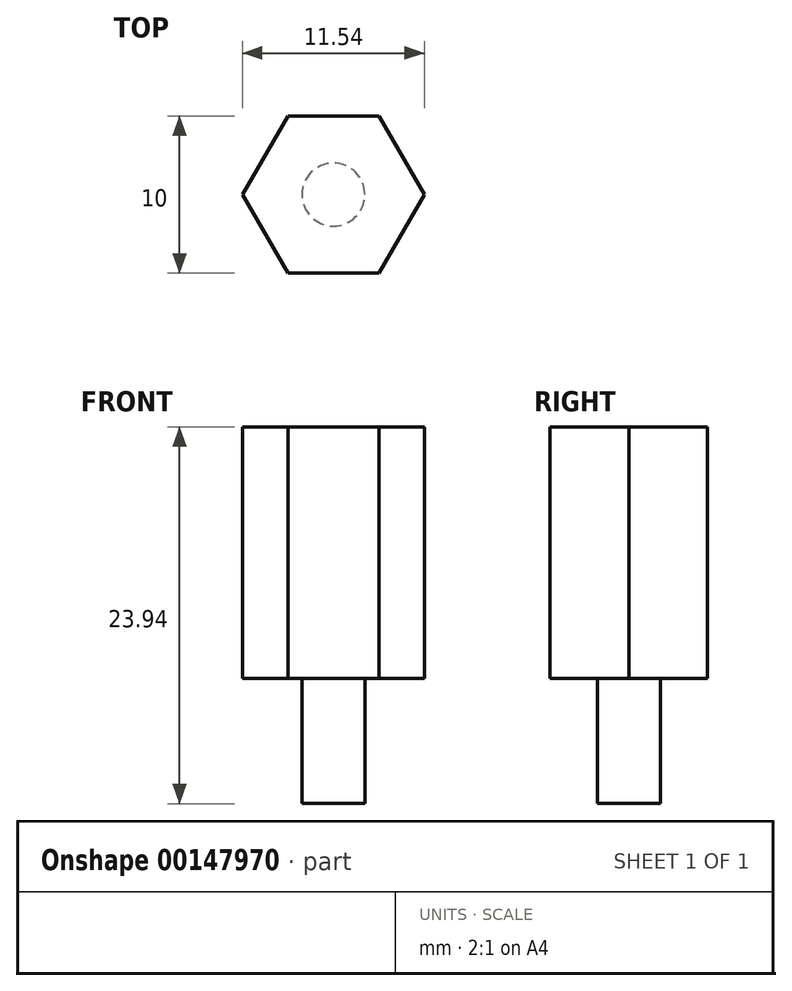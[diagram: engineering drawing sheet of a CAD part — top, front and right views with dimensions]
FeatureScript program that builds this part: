
annotation { "Feature Type Name" : "Feature", "Feature Type Description" : "" }
export const myFeature = defineFeature(function(context is Context, id is Id, definition is map)
    precondition{}
    {
        {
            var Q0;
            Q0=qCreatedBy(makeId("Top.planeOp"),FACE);
            var sketch = newSketch(context, id + "F0", { "sketchPlane" : qUnion([Q0])});
            skCircle(sketch, "E0.cCircle", {"center": v(0, 0) * mm, "radius": 5 * mm, "construction": true});
            skLineSegment(sketch, "E0.0", {"start": v(2.89, -5) * mm, "end": v(-2.89, -5) * mm});
            skLineSegment(sketch, "E0.1", {"start": v(-2.89, -5) * mm, "end": v(-5.77, 0) * mm});
            skLineSegment(sketch, "E0.2", {"start": v(-5.77, 0) * mm, "end": v(-2.89, 5) * mm});
            skLineSegment(sketch, "E0.3", {"start": v(-2.89, 5) * mm, "end": v(2.89, 5) * mm});
            skLineSegment(sketch, "E0.4", {"start": v(2.89, 5) * mm, "end": v(5.77, 0) * mm});
            skLineSegment(sketch, "E0.5", {"start": v(5.77, 0) * mm, "end": v(2.89, -5) * mm});
            skPoint(sketch, "E0.0.midPoint", {"position": v(0, -5) * mm});
            skSolve(sketch);
        }
        {
            var Q0;
            Q0=qSketchRegion(id+"F0",true);
            extrude(context, id + "F1", {"entities" : qUnion([Q0]), "depth" : 16 * mm});
        }
        {
            var Q0;
            Q0=makeQuery(id+"F1.opExtrude","CAP_FACE",FACE,{"disambiguationData":[OSD([sQuery(id+"F0.wireOp",EDGE,"E0.0"),sQuery(id+"F0.wireOp",EDGE,"E0.1"),sQuery(id+"F0.wireOp",EDGE,"E0.2"),sQuery(id+"F0.wireOp",EDGE,"E0.3"),sQuery(id+"F0.wireOp",EDGE,"E0.4"),sQuery(id+"F0.wireOp",EDGE,"E0.5")])],"isStart":true});
            var sketch = newSketch(context, id + "F2", { "sketchPlane" : qUnion([Q0])});
            skCircle(sketch, "E1", {"center": v(0, 0) * mm, "radius": 2 * mm});
            skSolve(sketch);
        }
        {
            var Q0;
            Q0=qSketchRegion(id+"F2",true);
            extrude(context, id + "F3", {"entities" : qUnion([Q0]), "operationType" : NewBodyOperationType.ADD, "depth" : 7.94 * mm});
        }
    });
